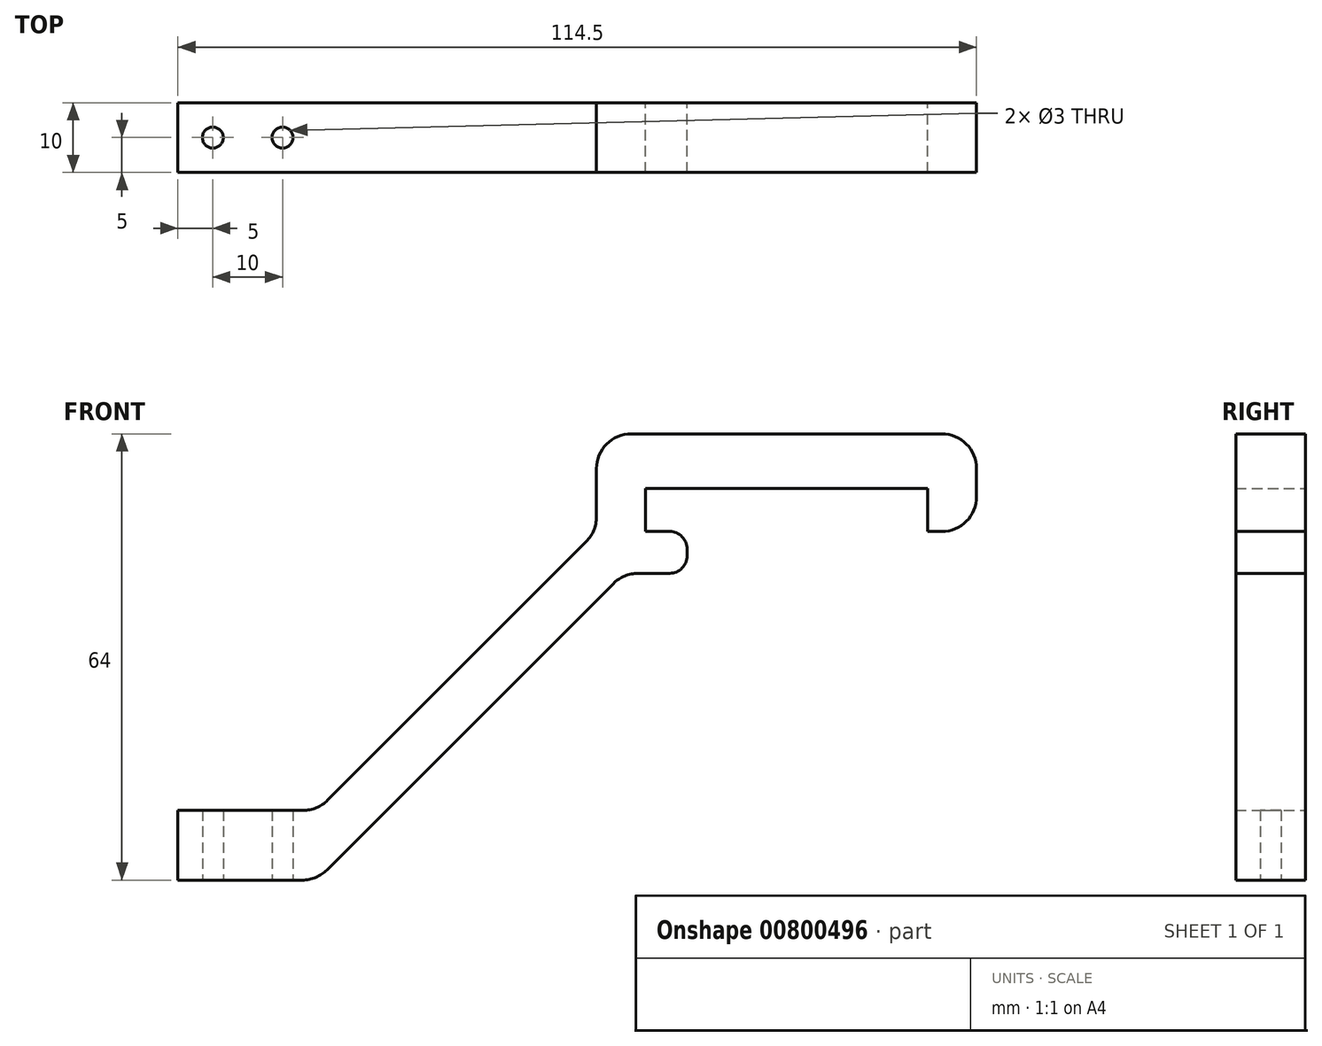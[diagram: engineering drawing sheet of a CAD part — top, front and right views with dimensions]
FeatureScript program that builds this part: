
annotation { "Feature Type Name" : "Feature", "Feature Type Description" : "" }
export const myFeature = defineFeature(function(context is Context, id is Id, definition is map)
    precondition{}
    {
        {
            var Q0;
            Q0=qCreatedBy(makeId("Front.planeOp"),FACE);
            var sketch = newSketch(context, id + "F0", { "sketchPlane" : qUnion([Q0])});
            skLineSegment(sketch, "E0.bottom", {"start": v(0, 0) * mm, "end": v(-40.5, 0) * mm});
            skLineSegment(sketch, "E0.top", {"start": v(-34.5, -6.2) * mm, "end": v(-40.5, -6.2) * mm});
            skLineSegment(sketch, "E0.left", {"start": v(0, 0) * mm, "end": v(0, -6.2) * mm});
            skLineSegment(sketch, "E0.right", {"start": v(-40.5, 0) * mm, "end": v(-40.5, -6.2) * mm});
            skLineSegment(sketch, "E1", {"start": v(0, -6.2) * mm, "end": v(7, -6.2) * mm});
            skLineSegment(sketch, "E2", {"start": v(7, -6.2) * mm, "end": v(7, 7.8) * mm});
            skLineSegment(sketch, "E3", {"start": v(-40.5, -6.2) * mm, "end": v(-34.5, -6.2) * mm});
            skLineSegment(sketch, "E4", {"start": v(-34.5, -6.2) * mm, "end": v(-34.5, -12.2) * mm});
            skLineSegment(sketch, "E5", {"start": v(7, 7.8) * mm, "end": v(-47.5, 7.8) * mm});
            skLineSegment(sketch, "E6", {"start": v(-47.5, 7.8) * mm, "end": v(-47.5, -6.2) * mm});
            skLineSegment(sketch, "E7", {"start": v(-47.5, -6.2) * mm, "end": v(-87.5, -46.2) * mm});
            skLineSegment(sketch, "E8", {"start": v(-87.5, -46.2) * mm, "end": v(-107.5, -46.2) * mm});
            skLineSegment(sketch, "E9", {"start": v(-107.5, -46.2) * mm, "end": v(-107.5, -56.2) * mm});
            skLineSegment(sketch, "E10", {"start": v(-107.5, -56.2) * mm, "end": v(-87.6, -56.2) * mm});
            skLineSegment(sketch, "E11", {"start": v(-43.6, -12.2) * mm, "end": v(-87.6, -56.2) * mm});
            skLineSegment(sketch, "E12", {"start": v(-34.5, -12.2) * mm, "end": v(-43.6, -12.2) * mm});
            skSolve(sketch);
        }
        {
            var Q0;
            Q0=makeQuery(id+"F0.imprint","IMPRINT",FACE,{"disambiguationData":[TD([[makeQuery(id+"F0.imprint","IMPRINT",EDGE,{"derivedFrom":sQuery(id+"F0.wireOp",EDGE,"E0.bottom")}),-1.0]])]});
            extrude(context, id + "F1", {"entities" : qUnion([Q0]), "depth" : 10 * mm, "offsetDistance" : 25 * mm});
        }
        {
            var Q0;
            Q0=makeQuery(id+"F1.opExtrude","SWEPT_EDGE",EDGE,{"disambiguationData":[OSD([sQuery(id+"F0.wireOp",EDGE,"E2"),sQuery(id+"F0.wireOp",EDGE,"EPbxDgAP-zYKe-liOF-gt3x-WyYanOSoHU68")])]});
            fillet(context, id + "F2", {"entities" : qUnion([Q0]), "radius" : 5 * mm, "tangentPropagation" : true, "allowEdgeOverflow" : false});
        }
        {
            var Q0;
            Q0=makeQuery(id+"F1.opExtrude","SWEPT_EDGE",EDGE,{"disambiguationData":[OSD([sQuery(id+"F0.wireOp",EDGE,"E4"),sQuery(id+"F0.wireOp",EDGE,"QVZ7E0rb-8Sd7-kk0w-n8ZD-7VhA22Bn5cac")])]});
            var Q1;
            Q1=makeQuery(id+"F1.opExtrude","SWEPT_EDGE",EDGE,{"disambiguationData":[OSD([sQuery(id+"F0.wireOp",EDGE,"QVZ7E0rb-8Sd7-kk0w-n8ZD-7VhA22Bn5cac"),sQuery(id+"F0.wireOp",EDGE,"04XB2HVS-MTA2-xwZm-yKOP-dUufRqHIiRfc")])]});
            fillet(context, id + "F3", {"entities" : qUnion([Q0, Q1]), "radius" : 2.5 * mm, "tangentPropagation" : true, "allowEdgeOverflow" : false});
        }
        {
            var Q0;
            Q0=makeQuery(id+"F1.opExtrude","SWEPT_EDGE",EDGE,{"disambiguationData":[OSD([sQuery(id+"F0.wireOp",EDGE,"E5"),sQuery(id+"F0.wireOp",EDGE,"E6")])]});
            var Q1;
            Q1=makeQuery(id+"F1.opExtrude","SWEPT_EDGE",EDGE,{"disambiguationData":[OSD([sQuery(id+"F0.wireOp",EDGE,"E6"),sQuery(id+"F0.wireOp",EDGE,"E7")])]});
            var Q2;
            Q2=makeQuery(id+"F1.opExtrude","SWEPT_EDGE",EDGE,{"disambiguationData":[OSD([sQuery(id+"F0.wireOp",EDGE,"E11"),sQuery(id+"F0.wireOp",EDGE,"E12")])]});
            var Q3;
            Q3=makeQuery(id+"F1.opExtrude","SWEPT_EDGE",EDGE,{"disambiguationData":[OSD([sQuery(id+"F0.wireOp",EDGE,"E7"),sQuery(id+"F0.wireOp",EDGE,"E8")])]});
            var Q4;
            Q4=makeQuery(id+"F1.opExtrude","SWEPT_EDGE",EDGE,{"disambiguationData":[OSD([sQuery(id+"F0.wireOp",EDGE,"E10"),sQuery(id+"F0.wireOp",EDGE,"E11")])]});
            fillet(context, id + "F4", {"entities" : qUnion([Q0, Q1, Q2, Q3, Q4]), "radius" : 5 * mm, "tangentPropagation" : true, "allowEdgeOverflow" : false});
        }
        {
            var Q0;
            Q0=makeQuery(id+"F1.opExtrude","SWEPT_FACE",FACE,{"disambiguationData":[OSD([sQuery(id+"F0.wireOp",EDGE,"E10")])]});
            var sketch = newSketch(context, id + "F5", { "sketchPlane" : qUnion([Q0])});
            skCircle(sketch, "E13", {"center": v(-102.5, 5) * mm, "radius": 1.5 * mm});
            skCircle(sketch, "E14", {"center": v(-92.5, 5) * mm, "radius": 1.5 * mm});
            skSolve(sketch);
        }
        {
            var Q0;
            Q0 = qSketchRegion(id + "F5", true);
            extrude(context, id + "F6", {"entities" : qUnion([Q0]), "operationType" : NewBodyOperationType.REMOVE, "oppositeDirection" : true, "depth" : 25 * mm, "offsetDistance" : 25 * mm});
        }
    });
